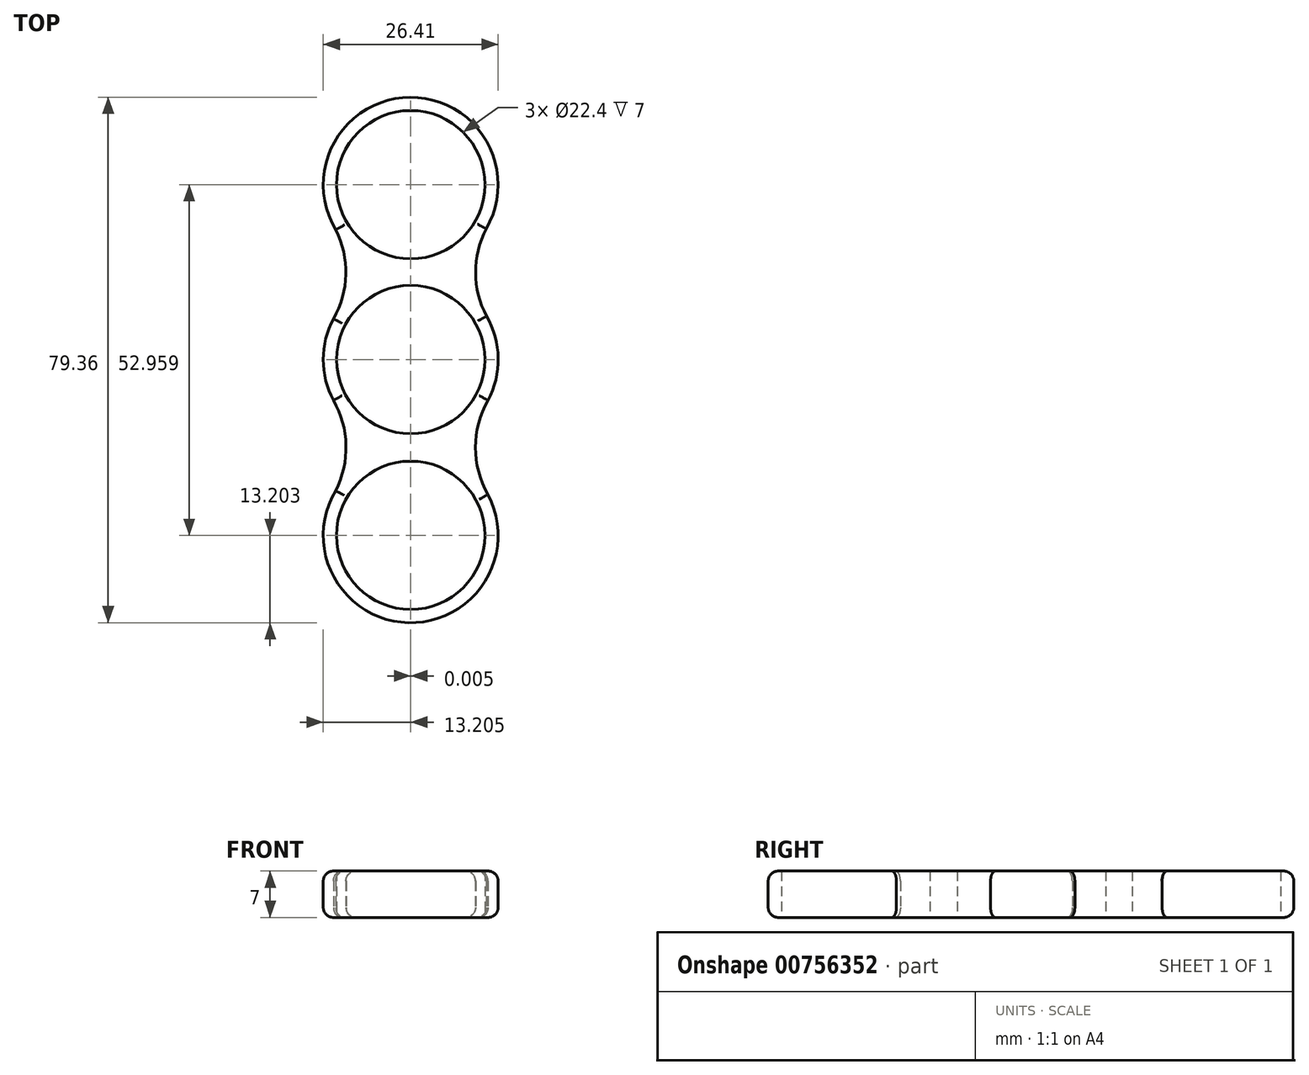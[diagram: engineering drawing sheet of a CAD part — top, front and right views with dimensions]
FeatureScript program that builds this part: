
annotation { "Feature Type Name" : "Feature", "Feature Type Description" : "" }
export const myFeature = defineFeature(function(context is Context, id is Id, definition is map)
    precondition{}
    {
        {
            var Q0;
            Q0=qCreatedBy(makeId("Top.planeOp"),FACE);
            var sketch = newSketch(context, id + "F0", { "sketchPlane" : qUnion([Q0])});
            skCircle(sketch, "E0", {"center": v(0, 0) * mm, "radius": 11.2 * mm});
            skArc(sketch, "E1", {"start": v(11.67, -6.17) * mm, "mid": v(13.2, 0.22) * mm, "end": v(11.46, 6.56) * mm});
            skCircle(sketch, "E2", {"center": v(0, 26.41) * mm, "radius": 11.2 * mm});
            skArc(sketch, "E3", {"start": v(11.38, 19.74) * mm, "mid": v(-0.08, 39.61) * mm, "end": v(-11.32, 19.62) * mm});
            skCircle(sketch, "E4.1.0", {"center": v(0, -26.55) * mm, "radius": 11.2 * mm});
            skArc(sketch, "E4.1.1", {"start": v(-11.35, -19.8) * mm, "mid": v(-0.34, -39.74) * mm, "end": v(11.67, -20.38) * mm});
            skPoint(sketch, "E4.center", {"position": v(0, -0.07) * mm});
            skArc(sketch, "E5", {"start": v(11.38, 19.74) * mm, "mid": v(9.8, 13.14) * mm, "end": v(11.46, 6.56) * mm});
            skArc(sketch, "E6.MirrorCS", {"start": v(-11.32, 19.62) * mm, "mid": v(-9.8, 12.85) * mm, "end": v(-11.67, 6.17) * mm});
            skArc(sketch, "E7", {"start": v(11.67, -6.17) * mm, "mid": v(9.77, -13.28) * mm, "end": v(11.67, -20.38) * mm});
            skArc(sketch, "E8.MirrorCS", {"start": v(-11.67, -6.17) * mm, "mid": v(-9.77, -12.94) * mm, "end": v(-11.35, -19.8) * mm});
            skArc(sketch, "E9.trimOffspring", {"start": v(-11.67, 6.17) * mm, "mid": v(-13.2, 0) * mm, "end": v(-11.67, -6.17) * mm});
            skPoint(sketch, "E10.orphan", {"position": v(-11.74, 20.38) * mm});
            skPoint(sketch, "E11.orphan", {"position": v(11.74, 20.38) * mm});
            skPoint(sketch, "E12.orphan", {"position": v(11.67, 6.17) * mm});
            skPoint(sketch, "E13.orphan", {"position": v(-11.67, -20.38) * mm});
            skSolve(sketch);
        }
        {
            var Q0;
            Q0=makeQuery(id+"F0.imprint","IMPRINT",FACE,{"disambiguationData":[TD([[makeQuery(id+"F0.imprint","IMPRINT",EDGE,{"derivedFrom":sQuery(id+"F0.wireOp",EDGE,"E0")}),-1.0]])]});
            extrude(context, id + "F1", {"entities" : qUnion([Q0]), "depth" : 7 * mm, "offsetDistance" : 25 * mm});
        }
        {
            var Q0;
            Q0=makeQuery(id+"F1.opExtrude","CAP_EDGE",EDGE,{"disambiguationData":[OSD([sQuery(id+"F0.wireOp",EDGE,"E8.MirrorCS")])],"isStart":false});
            var Q1;
            Q1=makeQuery(id+"F1.opExtrude","CAP_EDGE",EDGE,{"disambiguationData":[OSD([sQuery(id+"F0.wireOp",EDGE,"E4.1.1")])],"isStart":false});
            var Q2;
            Q2=makeQuery(id+"F1.opExtrude","CAP_EDGE",EDGE,{"disambiguationData":[OSD([sQuery(id+"F0.wireOp",EDGE,"E7")])],"isStart":false});
            var Q3;
            Q3=makeQuery(id+"F1.opExtrude","CAP_EDGE",EDGE,{"disambiguationData":[OSD([sQuery(id+"F0.wireOp",EDGE,"E1")])],"isStart":false});
            var Q4;
            Q4=makeQuery(id+"F1.opExtrude","CAP_EDGE",EDGE,{"disambiguationData":[OSD([sQuery(id+"F0.wireOp",EDGE,"E9.trimOffspring")])],"isStart":false});
            var Q5;
            Q5=makeQuery(id+"F1.opExtrude","CAP_EDGE",EDGE,{"disambiguationData":[OSD([sQuery(id+"F0.wireOp",EDGE,"E6.MirrorCS")])],"isStart":false});
            var Q6;
            Q6=makeQuery(id+"F1.opExtrude","CAP_EDGE",EDGE,{"disambiguationData":[OSD([sQuery(id+"F0.wireOp",EDGE,"E5")])],"isStart":false});
            var Q7;
            Q7=makeQuery(id+"F1.opExtrude","CAP_EDGE",EDGE,{"disambiguationData":[OSD([sQuery(id+"F0.wireOp",EDGE,"E3")])],"isStart":false});
            fillet(context, id + "F2", {"entities" : qUnion([Q0, Q1, Q2, Q3, Q4, Q5, Q6, Q7]), "radius" : 1.5 * mm, "tangentPropagation" : true, "allowEdgeOverflow" : false});
        }
        {
            var Q0;
            Q0=makeQuery(id+"F1.opExtrude","CAP_EDGE",EDGE,{"disambiguationData":[OSD([sQuery(id+"F0.wireOp",EDGE,"E3")])],"isStart":true});
            var Q1;
            Q1=makeQuery(id+"F1.opExtrude","CAP_EDGE",EDGE,{"disambiguationData":[OSD([sQuery(id+"F0.wireOp",EDGE,"E5")])],"isStart":true});
            var Q2;
            Q2=makeQuery(id+"F1.opExtrude","CAP_EDGE",EDGE,{"disambiguationData":[OSD([sQuery(id+"F0.wireOp",EDGE,"E6.MirrorCS")])],"isStart":true});
            var Q3;
            Q3=makeQuery(id+"F1.opExtrude","CAP_EDGE",EDGE,{"disambiguationData":[OSD([sQuery(id+"F0.wireOp",EDGE,"E1")])],"isStart":true});
            var Q4;
            Q4=makeQuery(id+"F1.opExtrude","CAP_EDGE",EDGE,{"disambiguationData":[OSD([sQuery(id+"F0.wireOp",EDGE,"E9.trimOffspring")])],"isStart":true});
            var Q5;
            Q5=makeQuery(id+"F1.opExtrude","CAP_EDGE",EDGE,{"disambiguationData":[OSD([sQuery(id+"F0.wireOp",EDGE,"E7")])],"isStart":true});
            var Q6;
            Q6=makeQuery(id+"F1.opExtrude","CAP_EDGE",EDGE,{"disambiguationData":[OSD([sQuery(id+"F0.wireOp",EDGE,"E8.MirrorCS")])],"isStart":true});
            var Q7;
            Q7=makeQuery(id+"F1.opExtrude","CAP_EDGE",EDGE,{"disambiguationData":[OSD([sQuery(id+"F0.wireOp",EDGE,"E4.1.1")])],"isStart":true});
            fillet(context, id + "F3", {"entities" : qUnion([Q0, Q1, Q2, Q3, Q4, Q5, Q6, Q7]), "radius" : 1.5 * mm, "tangentPropagation" : true, "allowEdgeOverflow" : false});
        }
    });
